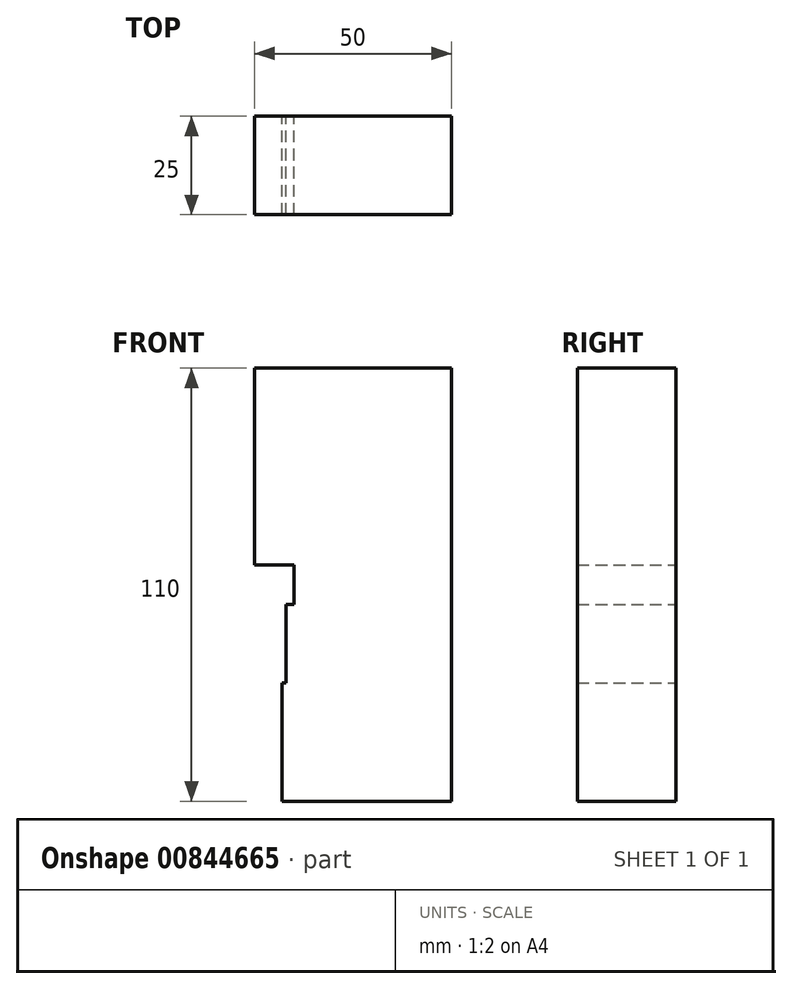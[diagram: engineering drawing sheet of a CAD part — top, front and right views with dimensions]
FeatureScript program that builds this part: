
annotation { "Feature Type Name" : "Feature", "Feature Type Description" : "" }
export const myFeature = defineFeature(function(context is Context, id is Id, definition is map)
    precondition{}
    {
        {
            var Q0;
            Q0=qCreatedBy(makeId("Front.planeOp"),FACE);
            var sketch = newSketch(context, id + "F0", { "sketchPlane" : qUnion([Q0])});
            skLineSegment(sketch, "E0.bottom", {"start": v(0, 0) * mm, "end": v(-40, 0) * mm});
            skLineSegment(sketch, "E0.top", {"start": v(0, 10) * mm, "end": v(-40, 10) * mm});
            skLineSegment(sketch, "E0.left", {"start": v(0, 0) * mm, "end": v(0, 10) * mm});
            skLineSegment(sketch, "E0.right", {"start": v(-40, 0) * mm, "end": v(-40, 10) * mm});
            skLineSegment(sketch, "E1.bottom", {"start": v(0, 10) * mm, "end": v(-50, 10) * mm});
            skLineSegment(sketch, "E1.top", {"start": v(0, 60) * mm, "end": v(-50, 60) * mm});
            skLineSegment(sketch, "E1.left", {"start": v(0, 10) * mm, "end": v(0, 60) * mm});
            skLineSegment(sketch, "E1.right", {"start": v(-50, 10) * mm, "end": v(-50, 60) * mm});
            skLineSegment(sketch, "E2.bottom", {"start": v(0, 0) * mm, "end": v(-42, 0) * mm});
            skLineSegment(sketch, "E2.top", {"start": v(0, -20) * mm, "end": v(-42, -20) * mm});
            skLineSegment(sketch, "E2.left", {"start": v(0, 0) * mm, "end": v(0, -20) * mm});
            skLineSegment(sketch, "E2.right", {"start": v(-42, 0) * mm, "end": v(-42, -20) * mm});
            skLineSegment(sketch, "E3.bottom", {"start": v(0, -20) * mm, "end": v(-43, -20) * mm});
            skLineSegment(sketch, "E3.top", {"start": v(0, -50) * mm, "end": v(-43, -50) * mm});
            skLineSegment(sketch, "E3.left", {"start": v(0, -20) * mm, "end": v(0, -50) * mm});
            skLineSegment(sketch, "E3.right", {"start": v(-43, -20) * mm, "end": v(-43, -50) * mm});
            skSolve(sketch);
        }
        {
            var Q0;
            Q0 = qSketchRegion(id + "F0", true);
            extrude(context, id + "F1", {"entities" : qUnion([Q0]), "depth" : 25 * mm, "offsetDistance" : 25 * mm});
        }
    });
